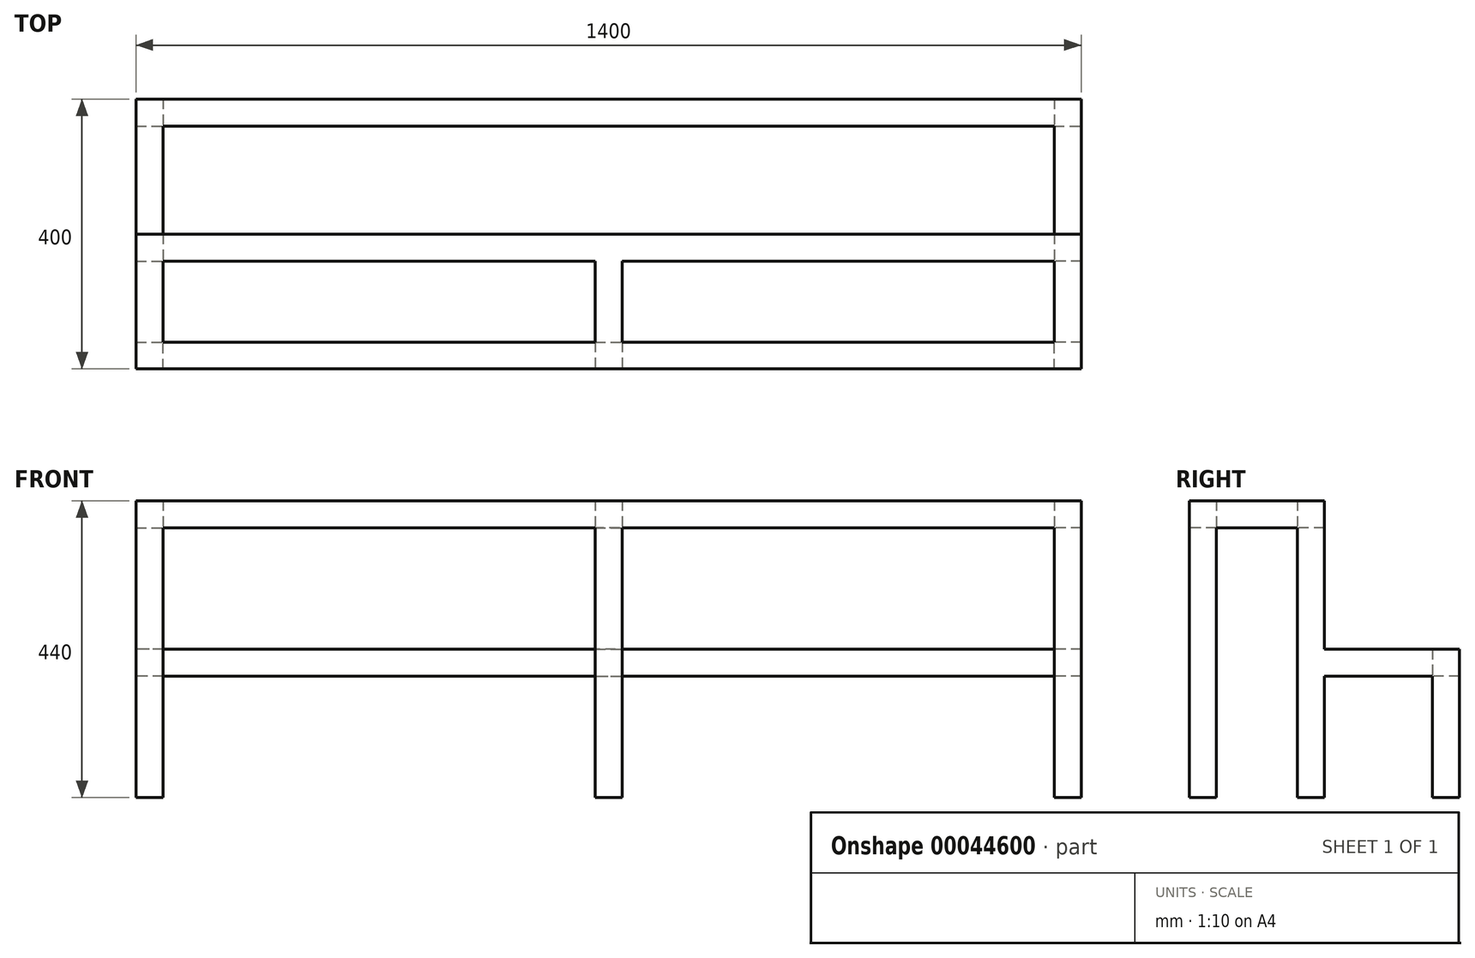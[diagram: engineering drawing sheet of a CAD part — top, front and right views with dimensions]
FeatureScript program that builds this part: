
annotation { "Feature Type Name" : "Feature", "Feature Type Description" : "" }
export const myFeature = defineFeature(function(context is Context, id is Id, definition is map)
    precondition{}
    {
        {
            var Q0;
            Q0=qCreatedBy(makeId("Top.planeOp"),FACE);
            var sketch = newSketch(context, id + "F0", { "sketchPlane" : qUnion([Q0])});
            skLineSegment(sketch, "E0.rect.bottom", {"start": v(700, 100) * mm, "end": v(-700, 100) * mm});
            skLineSegment(sketch, "E0.rect.top", {"start": v(700, -100) * mm, "end": v(-700, -100) * mm});
            skLineSegment(sketch, "E0.rect.left", {"start": v(700, 100) * mm, "end": v(700, -100) * mm});
            skLineSegment(sketch, "E0.rect.right", {"start": v(-700, 100) * mm, "end": v(-700, -100) * mm});
            skPoint(sketch, "E0.rect.middle", {"position": v(0, 0) * mm});
            skLineSegment(sketch, "E1.rect.bottom", {"start": v(660, 60) * mm, "end": v(-660, 60) * mm});
            skLineSegment(sketch, "E1.rect.top", {"start": v(660, -60) * mm, "end": v(-660, -60) * mm});
            skLineSegment(sketch, "E1.rect.left", {"start": v(660, 60) * mm, "end": v(660, -60) * mm});
            skLineSegment(sketch, "E1.rect.right", {"start": v(-660, 60) * mm, "end": v(-660, -60) * mm});
            skLineSegment(sketch, "E2", {"start": v(0, 60) * mm, "end": v(0, -60) * mm, "construction": true});
            skLineSegment(sketch, "E3", {"start": v(20, 60) * mm, "end": v(20, -60) * mm});
            skLineSegment(sketch, "E4", {"start": v(-20, 60) * mm, "end": v(-20, -60) * mm});
            skSolve(sketch);
        }
        {
            var Q0;
            Q0=makeQuery(id+"F0.imprint","IMPRINT",FACE,{"disambiguationData":[TD([[makeQuery(id+"F0.imprint","IMPRINT",EDGE,{"derivedFrom":sQuery(id+"F0.wireOp",EDGE,"E0.rect.bottom")}),1.0]])]});
            var Q1;
            {var subQ1=sQuery(id+"F0.wireOp",EDGE,"E3");Q1=makeQuery(id+"F0.imprint","IMPRINT",FACE,{"disambiguationData":[TD([[makeQuery(id+"F0.imprint","IMPRINT",EDGE,{"derivedFrom":subQ1}),-1.0]])]});}
            extrude(context, id + "F1", {"entities" : qUnion([Q0, Q1]), "depth" : 40 * mm});
        }
        {
            var Q0;
            Q0=makeQuery(id+"F1.opExtrude","CAP_FACE",FACE,{"disambiguationData":[OSD([sQuery(id+"F0.wireOp",EDGE,"E0.rect.bottom"),sQuery(id+"F0.wireOp",EDGE,"E0.rect.top"),sQuery(id+"F0.wireOp",EDGE,"E0.rect.left"),sQuery(id+"F0.wireOp",EDGE,"E0.rect.right"),sQuery(id+"F0.wireOp",EDGE,"E1.rect.bottom"),sQuery(id+"F0.wireOp",EDGE,"E1.rect.top"),sQuery(id+"F0.wireOp",EDGE,"E1.rect.left"),sQuery(id+"F0.wireOp",EDGE,"E1.rect.right"),sQuery(id+"F0.wireOp",EDGE,"E3"),sQuery(id+"F0.wireOp",EDGE,"E4")])],"isStart":true});
            var sketch = newSketch(context, id + "F2", { "sketchPlane" : qUnion([Q0])});
            skLineSegment(sketch, "E5.bottom", {"start": v(-700, 100) * mm, "end": v(-660, 100) * mm});
            skLineSegment(sketch, "E5.top", {"start": v(-700, 60) * mm, "end": v(-660, 60) * mm});
            skLineSegment(sketch, "E5.left", {"start": v(-700, 100) * mm, "end": v(-700, 60) * mm});
            skLineSegment(sketch, "E5.right", {"start": v(-660, 100) * mm, "end": v(-660, 60) * mm});
            skLineSegment(sketch, "E6.bottom", {"start": v(-700, -100) * mm, "end": v(-660, -100) * mm});
            skLineSegment(sketch, "E6.top", {"start": v(-700, -60) * mm, "end": v(-660, -60) * mm});
            skLineSegment(sketch, "E6.left", {"start": v(-700, -100) * mm, "end": v(-700, -60) * mm});
            skLineSegment(sketch, "E6.right", {"start": v(-660, -100) * mm, "end": v(-660, -60) * mm});
            skLineSegment(sketch, "E7.bottom", {"start": v(700, -100) * mm, "end": v(660, -100) * mm});
            skLineSegment(sketch, "E7.top", {"start": v(700, -60) * mm, "end": v(660, -60) * mm});
            skLineSegment(sketch, "E7.left", {"start": v(700, -100) * mm, "end": v(700, -60) * mm});
            skLineSegment(sketch, "E7.right", {"start": v(660, -100) * mm, "end": v(660, -60) * mm});
            skLineSegment(sketch, "E8.bottom", {"start": v(700, 100) * mm, "end": v(660, 100) * mm});
            skLineSegment(sketch, "E8.top", {"start": v(700, 60) * mm, "end": v(660, 60) * mm});
            skLineSegment(sketch, "E8.left", {"start": v(700, 100) * mm, "end": v(700, 60) * mm});
            skLineSegment(sketch, "E8.right", {"start": v(660, 100) * mm, "end": v(660, 60) * mm});
            skPoint(sketch, "E9.rect.middle", {"position": v(0, 0) * mm});
            skLineSegment(sketch, "E10.bottom", {"start": v(-20, -60) * mm, "end": v(20, -60) * mm});
            skLineSegment(sketch, "E10.top", {"start": v(-20, -100) * mm, "end": v(20, -100) * mm});
            skLineSegment(sketch, "E10.left", {"start": v(-20, -60) * mm, "end": v(-20, -100) * mm});
            skLineSegment(sketch, "E10.right", {"start": v(20, -60) * mm, "end": v(20, -100) * mm});
            skLineSegment(sketch, "E11.bottom", {"start": v(-20, 60) * mm, "end": v(20, 60) * mm});
            skLineSegment(sketch, "E11.top", {"start": v(-20, 100) * mm, "end": v(20, 100) * mm});
            skLineSegment(sketch, "E11.left", {"start": v(-20, 60) * mm, "end": v(-20, 100) * mm});
            skLineSegment(sketch, "E11.right", {"start": v(20, 60) * mm, "end": v(20, 100) * mm});
            skSolve(sketch);
        }
        {
            var Q0;
            Q0=makeQuery(id+"F2.imprint","IMPRINT",FACE,{"disambiguationData":[TD([[makeQuery(id+"F2.imprint","IMPRINT",EDGE,{"derivedFrom":sQuery(id+"F2.wireOp",EDGE,"E5.bottom")}),1.0]])]});
            var Q1;
            Q1=makeQuery(id+"F2.imprint","IMPRINT",FACE,{"disambiguationData":[TD([[makeQuery(id+"F2.imprint","IMPRINT",EDGE,{"derivedFrom":sQuery(id+"F2.wireOp",EDGE,"E6.bottom")}),-1.0]])]});
            var Q2;
            Q2=makeQuery(id+"F2.imprint","IMPRINT",FACE,{"disambiguationData":[TD([[makeQuery(id+"F2.imprint","IMPRINT",EDGE,{"derivedFrom":sQuery(id+"F2.wireOp",EDGE,"E9.rect.bottom")}),1.0]])]});
            var Q3;
            Q3=makeQuery(id+"F2.imprint","IMPRINT",FACE,{"disambiguationData":[TD([[makeQuery(id+"F2.imprint","IMPRINT",EDGE,{"derivedFrom":sQuery(id+"F2.wireOp",EDGE,"E8.bottom")}),1.0]])]});
            var Q4;
            Q4=makeQuery(id+"F2.imprint","IMPRINT",FACE,{"disambiguationData":[TD([[makeQuery(id+"F2.imprint","IMPRINT",EDGE,{"derivedFrom":sQuery(id+"F2.wireOp",EDGE,"E7.bottom")}),-1.0]])]});
            var Q5;
            Q5=makeQuery(id+"F2.imprint","IMPRINT",FACE,{"disambiguationData":[TD([[makeQuery(id+"F2.imprint","IMPRINT",EDGE,{"derivedFrom":sQuery(id+"F2.wireOp",EDGE,"E11.bottom")}),1.0]])]});
            extrude(context, id + "F3", {"entities" : qUnion([Q0, Q1, Q2, Q3, Q4, Q5]), "operationType" : NewBodyOperationType.ADD, "depth" : 400 * mm});
        }
        {
            var Q0;
            Q0=makeQuery(id+"F3.boolean.opBoolean","MERGE",FACE,{"derivedFrom":[makeQuery(id+"F1.opExtrude","SWEPT_FACE",FACE,{"disambiguationData":[OSD([sQuery(id+"F0.wireOp",EDGE,"E0.rect.bottom")])]}),makeQuery(id+"F3.opExtrude","SWEPT_FACE",FACE,{"disambiguationData":[OSD([sQuery(id+"F2.wireOp",EDGE,"E6.bottom")])]}),makeQuery(id+"F3.opExtrude","SWEPT_FACE",FACE,{"disambiguationData":[OSD([sQuery(id+"F2.wireOp",EDGE,"E7.bottom")])]}),makeQuery(id+"F3.opExtrude","SWEPT_FACE",FACE,{"disambiguationData":[OSD([sQuery(id+"F2.wireOp",EDGE,"E10.top")])]})]});
            var sketch = newSketch(context, id + "F4", { "sketchPlane" : qUnion([Q0])});
            skLineSegment(sketch, "E12.bottom", {"start": v(-700, -220) * mm, "end": v(-660, -220) * mm});
            skLineSegment(sketch, "E12.top", {"start": v(-700, -180) * mm, "end": v(-660, -180) * mm});
            skLineSegment(sketch, "E12.left", {"start": v(-660, -220) * mm, "end": v(-660, -180) * mm});
            skLineSegment(sketch, "E12.right", {"start": v(-700, -220) * mm, "end": v(-700, -180) * mm});
            skLineSegment(sketch, "E13.bottom", {"start": v(660, -180) * mm, "end": v(700, -180) * mm});
            skLineSegment(sketch, "E13.top", {"start": v(660, -220) * mm, "end": v(700, -220) * mm});
            skLineSegment(sketch, "E13.left", {"start": v(660, -180) * mm, "end": v(660, -220) * mm});
            skLineSegment(sketch, "E13.right", {"start": v(700, -180) * mm, "end": v(700, -220) * mm});
            skSolve(sketch);
        }
        {
            var Q0;
            Q0=makeQuery(id+"F4.imprint","IMPRINT",FACE,{"disambiguationData":[TD([[makeQuery(id+"F4.imprint","IMPRINT",EDGE,{"derivedFrom":sQuery(id+"F4.wireOp",EDGE,"E12.bottom")}),1.0]])]});
            var Q1;
            Q1=makeQuery(id+"F4.imprint","IMPRINT",FACE,{"disambiguationData":[TD([[makeQuery(id+"F4.imprint","IMPRINT",EDGE,{"derivedFrom":sQuery(id+"F4.wireOp",EDGE,"E13.bottom")}),-1.0]])]});
            extrude(context, id + "F5", {"entities" : qUnion([Q0, Q1]), "operationType" : NewBodyOperationType.ADD, "depth" : 200 * mm});
        }
        {
            var Q0;
            Q0=makeQuery(id+"F5.opExtrude","SWEPT_FACE",FACE,{"disambiguationData":[OSD([sQuery(id+"F4.wireOp",EDGE,"E13.top")])]});
            var sketch = newSketch(context, id + "F6", { "sketchPlane" : qUnion([Q0])});
            skLineSegment(sketch, "E14.bottom", {"start": v(-700, -300) * mm, "end": v(-660, -300) * mm});
            skLineSegment(sketch, "E14.top", {"start": v(-700, -260) * mm, "end": v(-660, -260) * mm});
            skLineSegment(sketch, "E14.left", {"start": v(-700, -260) * mm, "end": v(-700, -300) * mm});
            skLineSegment(sketch, "E14.right", {"start": v(-660, -260) * mm, "end": v(-660, -300) * mm});
            skSolve(sketch);
        }
        {
            var Q0;
            Q0=makeQuery(id+"F5.opExtrude","SWEPT_FACE",FACE,{"disambiguationData":[OSD([sQuery(id+"F4.wireOp",EDGE,"E12.bottom")])]});
            var sketch = newSketch(context, id + "F7", { "sketchPlane" : qUnion([Q0])});
            skLineSegment(sketch, "E15.bottom", {"start": v(660, -300) * mm, "end": v(700, -300) * mm});
            skLineSegment(sketch, "E15.top", {"start": v(660, -260) * mm, "end": v(700, -260) * mm});
            skLineSegment(sketch, "E15.left", {"start": v(660, -260) * mm, "end": v(660, -300) * mm});
            skLineSegment(sketch, "E15.right", {"start": v(700, -260) * mm, "end": v(700, -300) * mm});
            skSolve(sketch);
        }
        {
            var Q0;
            Q0=makeQuery(id+"F7.imprint","IMPRINT",FACE,{"disambiguationData":[TD([[makeQuery(id+"F7.imprint","IMPRINT",EDGE,{"derivedFrom":sQuery(id+"F7.wireOp",EDGE,"E15.bottom")}),-1.0]])]});
            var Q1;
            Q1=makeQuery(id+"F6.imprint","IMPRINT",FACE,{"disambiguationData":[TD([[makeQuery(id+"F6.imprint","IMPRINT",EDGE,{"derivedFrom":sQuery(id+"F6.wireOp",EDGE,"E14.bottom")}),-1.0]])]});
            extrude(context, id + "F8", {"entities" : qUnion([Q0, Q1]), "operationType" : NewBodyOperationType.ADD, "depth" : 180 * mm});
        }
        {
            var Q0;
            Q0=makeQuery(id+"F8.boolean.opBoolean","MERGE",FACE,{"derivedFrom":[makeQuery(id+"F5.boolean.opBoolean","MERGE",FACE,{"derivedFrom":[makeQuery(id+"F3.opExtrude","SWEPT_FACE",FACE,{"disambiguationData":[OSD([sQuery(id+"F2.wireOp",EDGE,"E7.right")])]}),makeQuery(id+"F5.opExtrude","SWEPT_FACE",FACE,{"disambiguationData":[OSD([sQuery(id+"F4.wireOp",EDGE,"E12.left")])]})]}),makeQuery(id+"F8.opExtrude","SWEPT_FACE",FACE,{"disambiguationData":[OSD([sQuery(id+"F7.wireOp",EDGE,"E15.left")])]})]});
            var sketch = newSketch(context, id + "F9", { "sketchPlane" : qUnion([Q0])});
            skLineSegment(sketch, "E16.bottom", {"start": v(-300, -180) * mm, "end": v(-260, -180) * mm});
            skLineSegment(sketch, "E16.top", {"start": v(-300, -220) * mm, "end": v(-260, -220) * mm});
            skLineSegment(sketch, "E16.left", {"start": v(-300, -180) * mm, "end": v(-300, -220) * mm});
            skLineSegment(sketch, "E16.right", {"start": v(-260, -180) * mm, "end": v(-260, -220) * mm});
            skSolve(sketch);
        }
        {
            var Q0;
            Q0=makeQuery(id+"F9.imprint","IMPRINT",FACE,{"disambiguationData":[TD([[makeQuery(id+"F9.imprint","IMPRINT",EDGE,{"derivedFrom":sQuery(id+"F9.wireOp",EDGE,"E16.bottom")}),-1.0]])]});
            extrude(context, id + "F10", {"entities" : qUnion([Q0]), "operationType" : NewBodyOperationType.ADD, "endBound" : BoundingType.UP_TO_NEXT, "depth" : 25 * mm});
        }
    });
